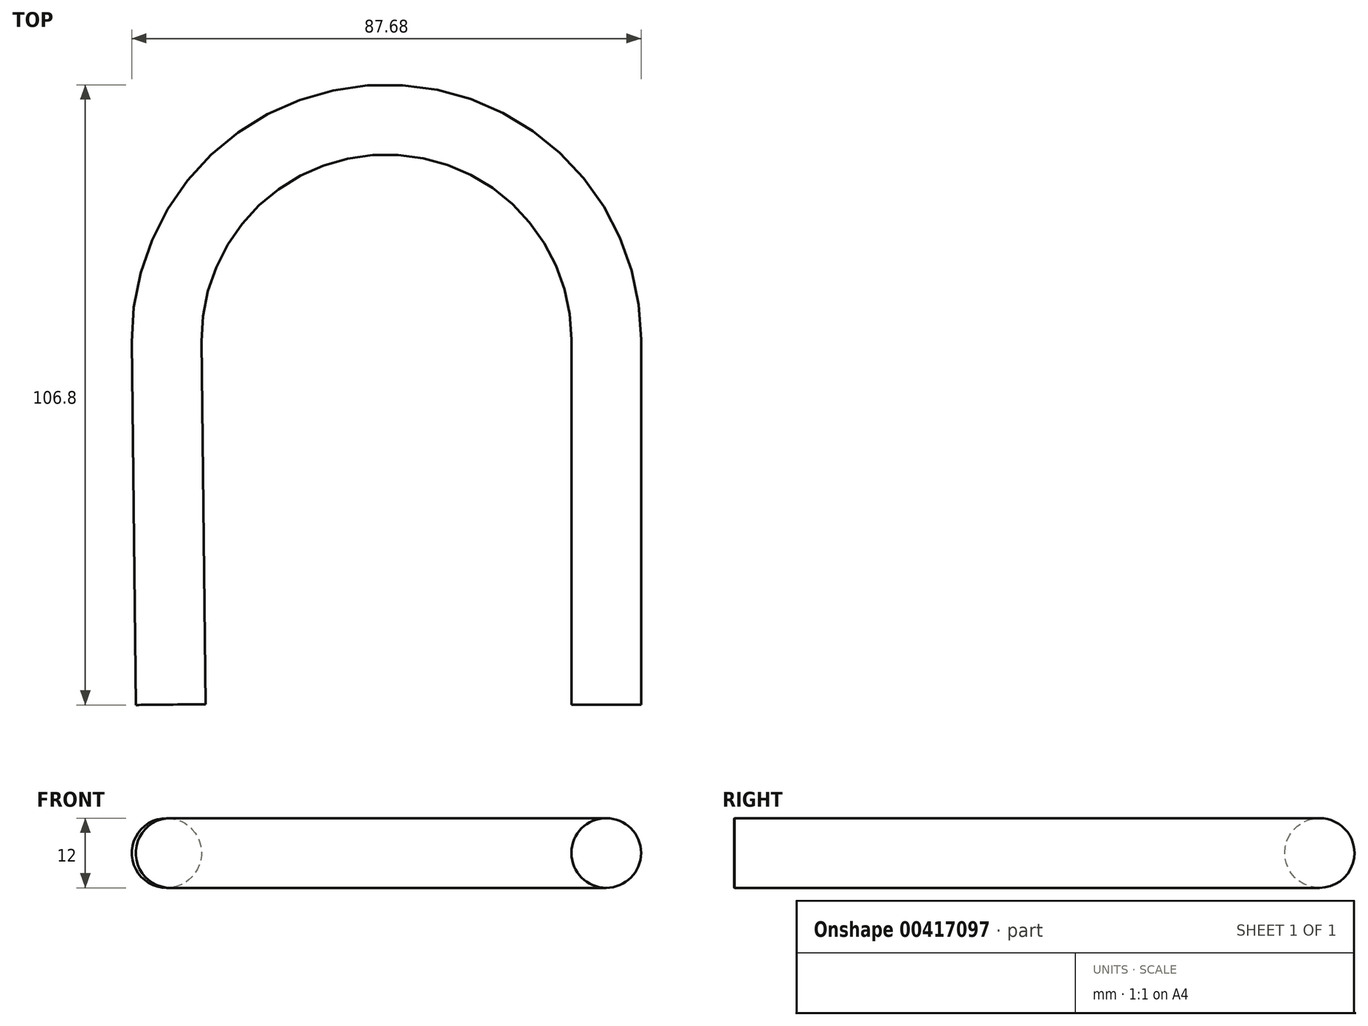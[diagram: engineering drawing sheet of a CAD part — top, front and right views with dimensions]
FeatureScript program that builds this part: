
annotation { "Feature Type Name" : "Feature", "Feature Type Description" : "" }
export const myFeature = defineFeature(function(context is Context, id is Id, definition is map)
    precondition{}
    {
        {
            var Q0;
            Q0=qCreatedBy(makeId("Top.planeOp"),FACE);
            var sketch = newSketch(context, id + "F0", { "sketchPlane" : qUnion([Q0])});
            skLineSegment(sketch, "E0", {"start": v(0, 0) * mm, "end": v(0, 62.9) * mm});
            skArc(sketch, "E1", {"start": v(0, 62.9) * mm, "mid": v(-38.04, 100.74) * mm, "end": v(-75.68, 62.5) * mm});
            skLineSegment(sketch, "E2", {"start": v(-75.68, 62.5) * mm, "end": v(-75, 0) * mm});
            skSolve(sketch);
        }
        {
            var Q0;
            Q0=qCreatedBy(makeId("Front.planeOp"),FACE);
            var sketch = newSketch(context, id + "F1", { "sketchPlane" : qUnion([Q0])});
            skCircle(sketch, "E3", {"center": v(0, 0) * mm, "radius": 6 * mm});
            skSolve(sketch);
        }
        {
            var Q0;
            Q0=makeQuery(id+"F1.imprint","IMPRINT",FACE,{"disambiguationData":[TD([[makeQuery(id+"F1.imprint","IMPRINT",EDGE,{"derivedFrom":sQuery(id+"F1.wireOp",EDGE,"E3")}),1.0]])]});
            var Q1;
            Q1=sQuery(id+"F0.wireOp",EDGE,"E0");
            var Q2;
            Q2=sQuery(id+"F0.wireOp",EDGE,"E1");
            var Q3;
            Q3=sQuery(id+"F0.wireOp",EDGE,"E2");
            sweep(context, id + "F2", {"profiles" : qUnion([Q0]), "path" : qUnion([Q1, Q2, Q3])});
        }
    });
